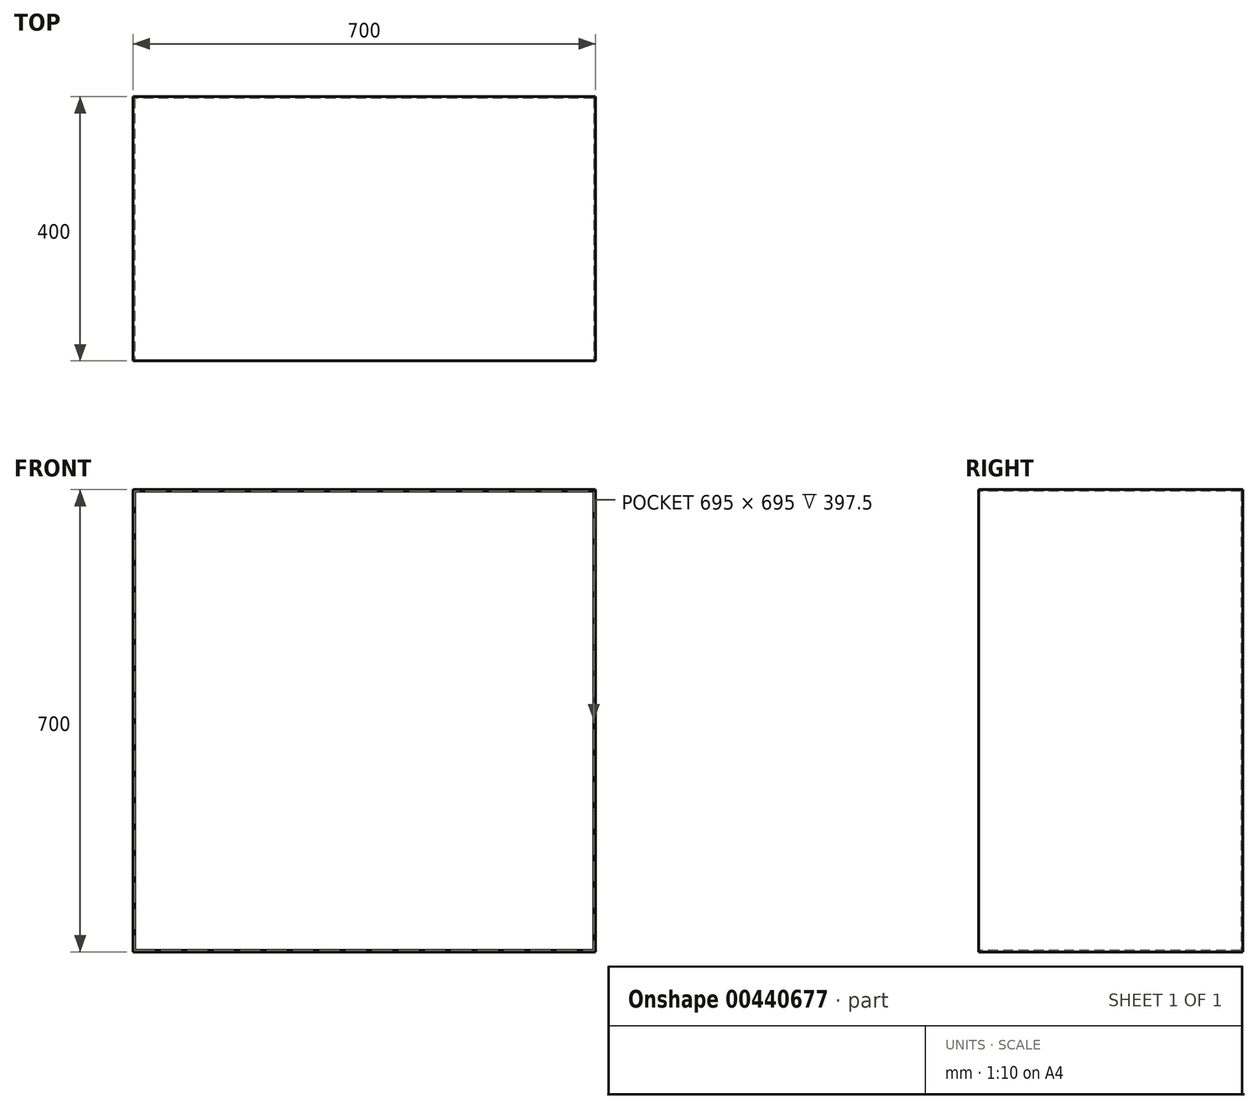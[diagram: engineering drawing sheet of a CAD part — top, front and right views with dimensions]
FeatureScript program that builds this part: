
annotation { "Feature Type Name" : "Feature", "Feature Type Description" : "" }
export const myFeature = defineFeature(function(context is Context, id is Id, definition is map)
    precondition{}
    {
        {
            assignVariable(context, id + "F0", {"name" : "HEIGHT", "anyValue" : 700});
        }
        {
            var Q0;
            Q0=qCreatedBy(makeId("Top.planeOp"),FACE);
            var sketch = newSketch(context, id + "F1", { "sketchPlane" : qUnion([Q0])});
            skLineSegment(sketch, "E0.bottom", {"start": v(374.48, 200) * mm, "end": v(-325.52, 200) * mm});
            skLineSegment(sketch, "E0.top", {"start": v(374.48, -200) * mm, "end": v(-325.52, -200) * mm});
            skLineSegment(sketch, "E0.left", {"start": v(374.48, 200) * mm, "end": v(374.48, -200) * mm});
            skLineSegment(sketch, "E0.right", {"start": v(-325.52, 200) * mm, "end": v(-325.52, -200) * mm});
            skPoint(sketch, "E0.middle", {"position": v(24.48, 0) * mm});
            skSolve(sketch);
        }
        {
            var Q0;
            Q0 = qSketchRegion(id + "F1", true);
            extrude(context, id + "F2", {"entities" : qUnion([Q0]), "depth" : (getVariable(context, 'HEIGHT')) * mm});
        }
        {
            var Q0;
            Q0=makeQuery(id+"F2.opExtrude","SWEPT_FACE",FACE,{"disambiguationData":[OSD([sQuery(id+"F1.wireOp",EDGE,"E0.top")])]});
            shell(context, id + "F3", {"entities" : qUnion([Q0]), "thickness" : 2.5 * mm});
        }
    });
